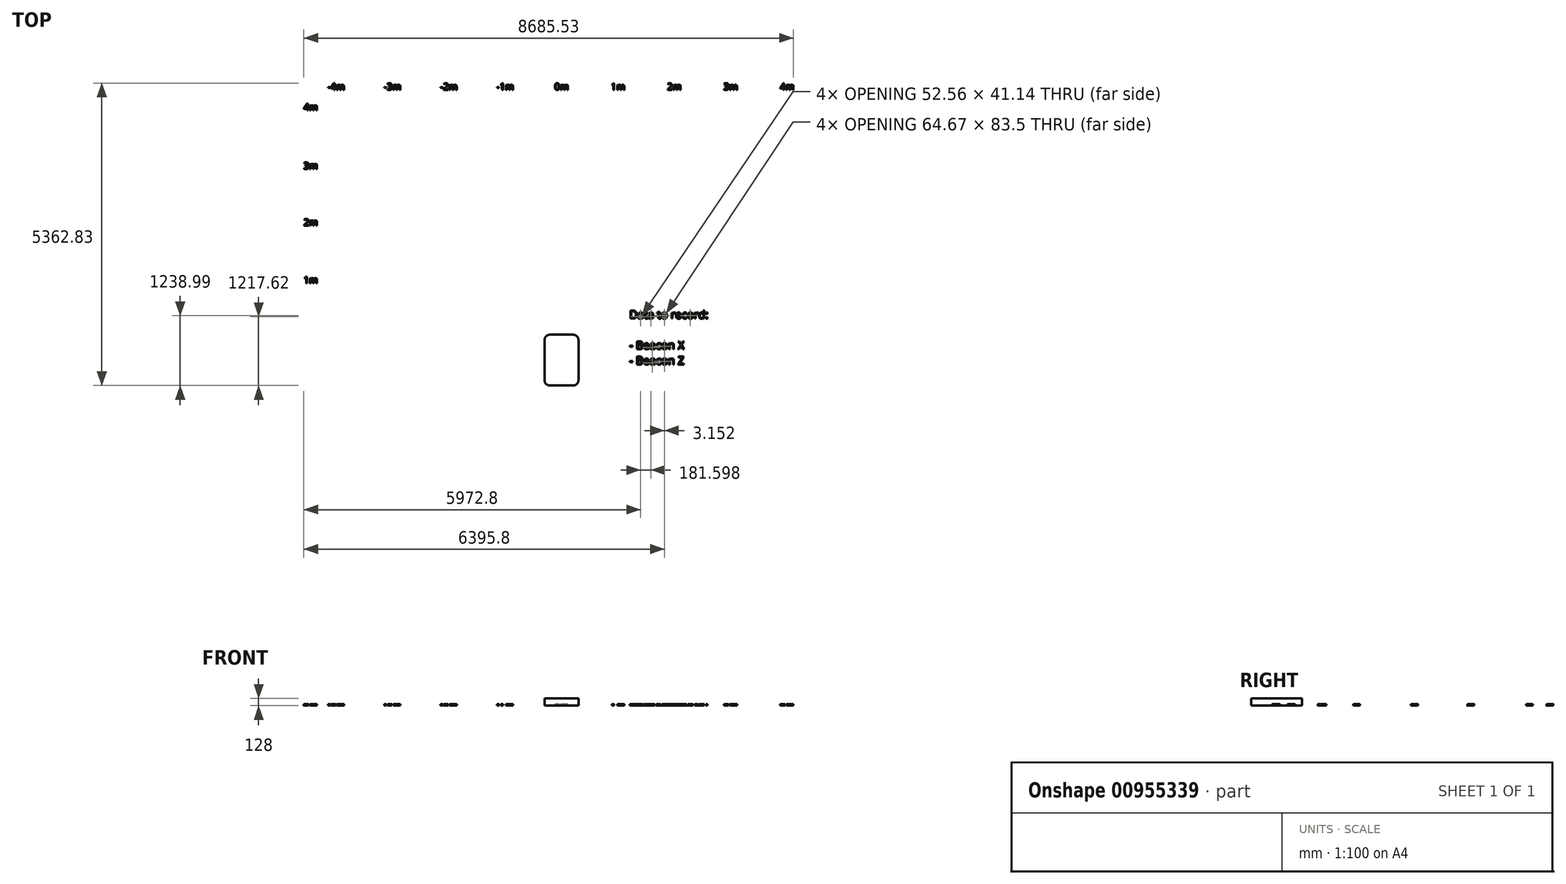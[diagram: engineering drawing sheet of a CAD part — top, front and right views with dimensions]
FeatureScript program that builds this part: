
annotation { "Feature Type Name" : "Feature", "Feature Type Description" : "" }
export const myFeature = defineFeature(function(context is Context, id is Id, definition is map)
    precondition{}
    {
        {
            var Q0;
            Q0=qCreatedBy(makeId("Top.planeOp"),FACE);
            var sketch = newSketch(context, id + "F0", { "sketchPlane" : qUnion([Q0])});
            skLineSegment(sketch, "E0.bottom", {"start": v(-210, 0) * mm, "end": v(210, 0) * mm});
            skLineSegment(sketch, "E0.top", {"start": v(-210, -900) * mm, "end": v(210, -900) * mm});
            skLineSegment(sketch, "E0.left", {"start": v(-300, -90) * mm, "end": v(-300, -810) * mm});
            skLineSegment(sketch, "E0.right", {"start": v(300, -90) * mm, "end": v(300, -810) * mm});
            skPoint(sketch, "E1.visualSharp", {"position": v(-300, 0) * mm});
            skArc(sketch, "E1.filletArc", {"start": v(-210, 0) * mm, "mid": v(-273.64, -26.36) * mm, "end": v(-300, -90) * mm});
            skPoint(sketch, "E2.visualSharp", {"position": v(-300, -900) * mm});
            skArc(sketch, "E2.filletArc", {"start": v(-300, -810) * mm, "mid": v(-273.64, -873.64) * mm, "end": v(-210, -900) * mm});
            skPoint(sketch, "E3.visualSharp", {"position": v(300, 0) * mm});
            skArc(sketch, "E3.filletArc", {"start": v(300, -90) * mm, "mid": v(273.64, -26.36) * mm, "end": v(210, 0) * mm});
            skPoint(sketch, "E4.visualSharp", {"position": v(300, -900) * mm});
            skArc(sketch, "E4.filletArc", {"start": v(210, -900) * mm, "mid": v(273.64, -873.64) * mm, "end": v(300, -810) * mm});
            skSolve(sketch);
        }
        {
            var Q0;
            Q0 = qSketchRegion(id + "F0", true);
            extrude(context, id + "F1", {"entities" : qUnion([Q0]), "depth" : 128 * mm, "offsetDistance" : 25 * mm});
        }
        {
            var Q0;
            Q0=qCreatedBy(makeId("Top.planeOp"),FACE);
            var sketch = newSketch(context, id + "F2", { "sketchPlane" : qUnion([Q0])});
            skLineSegment(sketch, "E5", {"start": v(0, 0) * mm, "end": v(0, 4000) * mm, "construction": true});
            skLineSegment(sketch, "E6", {"start": v(-4000, 1000) * mm, "end": v(4000, 1000) * mm, "construction": true});
            skLineSegment(sketch, "E7", {"start": v(-4000, 2000) * mm, "end": v(4000, 2000) * mm, "construction": true});
            skLineSegment(sketch, "E8", {"start": v(-4000, 3000) * mm, "end": v(4000, 3000) * mm, "construction": true});
            skLineSegment(sketch, "E9", {"start": v(-4000, 4000) * mm, "end": v(4000, 4000) * mm, "construction": true});
            skLineSegment(sketch, "E10", {"start": v(-1000, 4000) * mm, "end": v(-1000, 1000) * mm, "construction": true});
            skLineSegment(sketch, "E11", {"start": v(-2000, 4000) * mm, "end": v(-2000, 1000) * mm, "construction": true});
            skLineSegment(sketch, "E12", {"start": v(-3000, 4000) * mm, "end": v(-3000, 1000) * mm, "construction": true});
            skLineSegment(sketch, "E13", {"start": v(-4000, 4000) * mm, "end": v(-4000, 1000) * mm, "construction": true});
            skLineSegment(sketch, "E14", {"start": v(4000, 4000) * mm, "end": v(4000, 1000) * mm, "construction": true});
            skLineSegment(sketch, "E15", {"start": v(3000, 4000) * mm, "end": v(3000, 1000) * mm, "construction": true});
            skLineSegment(sketch, "E16", {"start": v(2000, 4000) * mm, "end": v(2000, 1000) * mm, "construction": true});
            skLineSegment(sketch, "E17", {"start": v(1000, 4000) * mm, "end": v(1000, 1000) * mm, "construction": true});
            skPoint(sketch, "E18", {"position": v(-3000, 3000) * mm});
            skPoint(sketch, "E19", {"position": v(-3000, 2000) * mm});
            skPoint(sketch, "E20", {"position": v(-2000, 2000) * mm});
            skPoint(sketch, "E21", {"position": v(-2000, 3000) * mm});
            skPoint(sketch, "E22", {"position": v(-1000, 3000) * mm});
            skPoint(sketch, "E23", {"position": v(-1000, 2000) * mm});
            skPoint(sketch, "E24", {"position": v(0, 2000) * mm});
            skPoint(sketch, "E25", {"position": v(0, 3000) * mm});
            skPoint(sketch, "E26", {"position": v(1000, 3000) * mm});
            skPoint(sketch, "E27", {"position": v(1000, 2000) * mm});
            skPoint(sketch, "E28", {"position": v(2000, 2000) * mm});
            skPoint(sketch, "E29", {"position": v(2000, 3000) * mm});
            skPoint(sketch, "E30", {"position": v(3000, 3000) * mm});
            skPoint(sketch, "E31", {"position": v(3000, 2000) * mm});
            skPoint(sketch, "E32", {"position": v(0, 1000) * mm});
            skSolve(sketch);
        }
        {
            var Q0;
            Q0=qCreatedBy(makeId("Top.planeOp"),FACE);
            var sketch = newSketch(context, id + "F3", { "sketchPlane" : qUnion([Q0])});
            skText(sketch, "E33", { "text": "1m", "fontName": "OpenSans-Regular.ttf"});
            skText(sketch, "E34", { "text": "2m", "fontName": "OpenSans-Regular.ttf"});
            skText(sketch, "E35", { "text": "3m", "fontName": "OpenSans-Regular.ttf"});
            skText(sketch, "E36", { "text": "4m", "fontName": "OpenSans-Regular.ttf"});
            skText(sketch, "E37", { "text": "1m", "fontName": "OpenSans-Regular.ttf"});
            skText(sketch, "E38", { "text": "2m", "fontName": "OpenSans-Regular.ttf"});
            skText(sketch, "E39", { "text": "3m", "fontName": "OpenSans-Regular.ttf"});
            skText(sketch, "E40", { "text": "4m", "fontName": "OpenSans-Regular.ttf"});
            skText(sketch, "E41", { "text": "-1m", "fontName": "OpenSans-Regular.ttf"});
            skText(sketch, "E42", { "text": "-2m", "fontName": "OpenSans-Regular.ttf"});
            skText(sketch, "E43", { "text": "-3m", "fontName": "OpenSans-Regular.ttf"});
            skText(sketch, "E44", { "text": "-4m", "fontName": "OpenSans-Regular.ttf"});
            skText(sketch, "E45", { "text": "0m", "fontName": "OpenSans-Regular.ttf"});
            const initialGuessF3  = {"E33": [-4.57496, 0.9119, 1, 0, 0.12116], "E34": [-4.57496, 1.93474, 1, 0, 0.12116], "E35": [-4.57496, 2.93714, 1, 0, 0.12116], "E36": [-4.57496, 3.9762, 1, 0, 0.12116], "E37": [0.875, 4.3408, 1, 0, 0.12116], "E38": [1.875, 4.3408, 1, 0, 0.12116], "E39": [2.875, 4.3408, 1, 0, 0.12116], "E40": [3.875, 4.3408, 1, 0, 0.12116], "E41": [-1.15207, 4.3408, 1, 0, 0.12116], "E42": [-2.15207, 4.3408, 1, 0, 0.12116], "E43": [-3.15207, 4.3408, 1, 0, 0.12116], "E44": [-4.15207, 4.3408, 1, 0, 0.12116], "E45": [-0.125, 4.3408, 1, 0, 0.12116]};
            skSetInitialGuess(sketch, initialGuessF3);
            skSolve(sketch);
        }
        {
            var Q0;
            Q0 = qSketchRegion(id + "F3", true);
            extrude(context, id + "F4", {"entities" : qUnion([Q0]), "depth" : 25 * mm, "offsetDistance" : 25 * mm});
        }
        {
            var Q0;
            Q0=qCreatedBy(makeId("Top.planeOp"),FACE);
            var sketch = newSketch(context, id + "F5", { "sketchPlane" : qUnion([Q0])});
            skText(sketch, "E46", { "text": "Data to record:\n\n- Beacon X\n- Beacon Z", "fontName": "OpenSans-Regular.ttf"});
            const initialGuessF5  = {"E46": [1.20328, 0.28563, 1, 0, 0.14383]};
            skSetInitialGuess(sketch, initialGuessF5);
            skSolve(sketch);
        }
        {
            var Q0;
            Q0 = qSketchRegion(id + "F5", true);
            extrude(context, id + "F6", {"entities" : qUnion([Q0]), "depth" : 25 * mm, "offsetDistance" : 25 * mm});
        }
    });
